# Revit family: Ball_Valve-Zurn_Wilkins-Model_850XL_Threaded-(0.5-2_Inch)
name_source: partatom
category: Pipe Accessories
revit_build: Autodesk Revit 2015 (Build: 20140606_1530(x64)
units: mm (PartAtom-declared; Revit-internal decimal feet)

## types (6) — shared parameters
Assembly Code = D2090800
Description = Lead-Free* Ball Valve
Flow = 0 GPM
Manufacturer = Zurn Wilkins
Model = 850XL
Pressure Rating = 600 psi WOG
Product Page URL = http://www.zurn.com
Product data url = https://bimobject.com
Specification Sheet URL = http://content.zurn.com
Temp Rating = 33F - 350F @ 50 psi
Type Comments = Threaded Connections ANSI B1.20.1
URL = http://www.zurn.com

## per-type parameters (varying)
| type | Body Diameter | Body Length | Body Radius | Handle Height | Handle Length | Handle Lever | Handle Wheel | Length | Nominal Diameter | Nominal Radius | Tap Size FNPT | Thread FNPT | Thread MNPT | Weight |
| 2" | 0' - 3" | 0' - 4 1/2" | 0' - 1 1/2" | 0' - 3 7/8" | 0' - 4 3/4" | Yes | No | 0' - 4 1/2" | 0' - 2" | 0' - 1" | 1/4-18 | 2-11 1/2 |  | 6 lbs. |
| 1 1/2" | 0' - 2 1/2" | 0' - 3 3/4" | 0' - 1 1/4" | 0' - 2 7/8" | 0' - 4 3/4" | Yes | No | 0' - 3 3/4" | 0' - 1 1/2" | 0' - 0 3/4" | 1/4-18 | 1 1/2-11 1/2 |  | 3 lbs. |
| 1 1/4" | 0' - 2 1/4" | 0' - 3 5/16" | 0' - 1 1/8" | 0' - 2 5/8" | 0' - 3 1/2" | Yes | No | 0' - 3 5/16" | 0' - 1 1/4" | 0' - 0 5/8" | 1/4-18 | 1 1/4-11 1/2 |  | 3 lbs. |
| 1" | 0' - 2" | 0' - 2 3/4" | 0' - 1" | 0' - 2" | 0' - 1 5/8" | No | Yes | 0' - 2 3/4" | 0' - 1" | 0' - 0 1/2" | 1/8-27 | 1-11 1/2 |  | 2 lbs. |
| 3/4" | 0' - 1 3/4" | 0' - 2 1/2" | 0' - 0 7/8" | 0' - 1 3/4" | 0' - 1 5/8" | No | Yes | 0' - 2 1/2" | 0' - 0 3/4" | 0' - 0 3/8" | 1/8-27 | 3/4-14 |  | 1 lbs. |
| 1/2" | 0' - 1 1/2" | 0' - 2 1/4" | 0' - 0 3/4" | 0' - 1 7/8" | 0' - 2 3/4" | Yes | No | 0' - 2 1/4" | 0' - 0 1/2" | 0' - 0 1/4" | 1/8-27 | 1/2-14 | 1/2-14 | 1 lbs. |

## geometry (parser evidence)
native form markers: Sweep x6
no freeform markers — native parametric forms only
